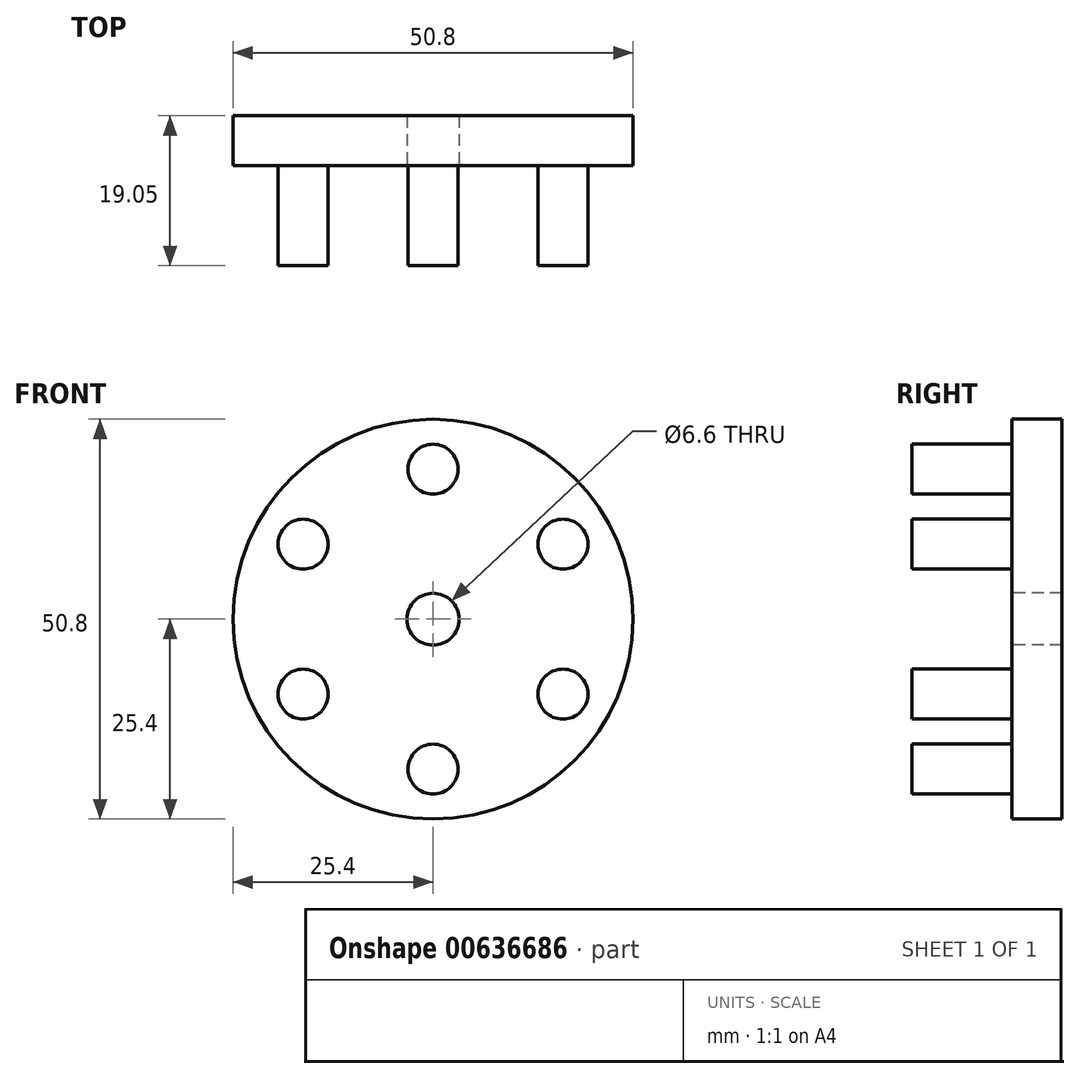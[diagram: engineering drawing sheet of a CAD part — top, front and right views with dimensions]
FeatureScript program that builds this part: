
annotation { "Feature Type Name" : "Feature", "Feature Type Description" : "" }
export const myFeature = defineFeature(function(context is Context, id is Id, definition is map)
    precondition{}
    {
        {
            var Q0;
            Q0=qCreatedBy(makeId("Front.planeOp"),FACE);
            var sketch = newSketch(context, id + "F0", { "sketchPlane" : qUnion([Q0])});
            skCircle(sketch, "E0", {"center": v(0, 0) * mm, "radius": 25.4 * mm});
            skSolve(sketch);
        }
        {
            var Q0;
            Q0 = qSketchRegion(id + "F0", true);
            extrude(context, id + "F1", {"entities" : qUnion([Q0]), "depth" : 6.35 * mm, "offsetDistance" : 25.4 * mm});
        }
        {
            var Q0;
            Q0=makeQuery(id+"F1.opExtrude","CAP_FACE",FACE,{"disambiguationData":[OSD([sQuery(id+"F0.wireOp",EDGE,"E0")])],"isStart":false});
            var sketch = newSketch(context, id + "F2", { "sketchPlane" : qUnion([Q0])});
            skLineSegment(sketch, "E1", {"start": v(0, 25.4) * mm, "end": v(0, 19.05) * mm, "construction": true});
            skCircle(sketch, "E2", {"center": v(0, 19.05) * mm, "radius": 3.18 * mm});
            skCircle(sketch, "E3.1.0", {"center": v(-16.5, 9.53) * mm, "radius": 3.18 * mm});
            skCircle(sketch, "E3.2.0", {"center": v(-16.5, -9.52) * mm, "radius": 3.18 * mm});
            skCircle(sketch, "E3.3.0", {"center": v(0, -19.05) * mm, "radius": 3.18 * mm});
            skCircle(sketch, "E3.4.0", {"center": v(16.5, -9.53) * mm, "radius": 3.18 * mm});
            skCircle(sketch, "E3.5.0", {"center": v(16.5, 9.53) * mm, "radius": 3.18 * mm});
            skPoint(sketch, "E3.center", {"position": v(0, 0) * mm});
            skCircle(sketch, "E4", {"center": v(0, 0) * mm, "radius": 3.3 * mm});
            skSolve(sketch);
        }
        {
            var Q0;
            Q0=makeQuery(id+"F2.imprint","IMPRINT",FACE,{"disambiguationData":[TD([[makeQuery(id+"F2.imprint","IMPRINT",EDGE,{"derivedFrom":sQuery(id+"F2.wireOp",EDGE,"E3.2.0")}),1.0]])]});
            var Q1;
            Q1=makeQuery(id+"F2.imprint","IMPRINT",FACE,{"disambiguationData":[TD([[makeQuery(id+"F2.imprint","IMPRINT",EDGE,{"derivedFrom":sQuery(id+"F2.wireOp",EDGE,"E3.3.0")}),1.0]])]});
            var Q2;
            Q2=makeQuery(id+"F2.imprint","IMPRINT",FACE,{"disambiguationData":[TD([[makeQuery(id+"F2.imprint","IMPRINT",EDGE,{"derivedFrom":sQuery(id+"F2.wireOp",EDGE,"E3.4.0")}),1.0]])]});
            var Q3;
            Q3=makeQuery(id+"F2.imprint","IMPRINT",FACE,{"disambiguationData":[TD([[makeQuery(id+"F2.imprint","IMPRINT",EDGE,{"derivedFrom":sQuery(id+"F2.wireOp",EDGE,"E3.5.0")}),1.0]])]});
            var Q4;
            Q4=makeQuery(id+"F2.imprint","IMPRINT",FACE,{"disambiguationData":[TD([[makeQuery(id+"F2.imprint","IMPRINT",EDGE,{"derivedFrom":sQuery(id+"F2.wireOp",EDGE,"E3.1.0")}),1.0]])]});
            var Q5;
            Q5=makeQuery(id+"F2.imprint","IMPRINT",FACE,{"disambiguationData":[TD([[makeQuery(id+"F2.imprint","IMPRINT",EDGE,{"derivedFrom":sQuery(id+"F2.wireOp",EDGE,"E2")}),1.0]])]});
            extrude(context, id + "F3", {"entities" : qUnion([Q0, Q1, Q2, Q3, Q4, Q5]), "depth" : 12.7 * mm, "offsetDistance" : 25.4 * mm});
        }
        {
            var Q0;
            Q0=makeQuery(id+"F1.opExtrude","CAP_FACE",FACE,{"disambiguationData":[OSD([sQuery(id+"F0.wireOp",EDGE,"E0")])],"isStart":false});
            var sketch = newSketch(context, id + "F4", { "sketchPlane" : qUnion([Q0])});
            skCircle(sketch, "E5", {"center": v(0, 0) * mm, "radius": 3.3 * mm});
            skSolve(sketch);
        }
        {
            var Q0;
            Q0 = qSketchRegion(id + "F4", true);
            extrude(context, id + "F5", {"entities" : qUnion([Q0]), "operationType" : NewBodyOperationType.REMOVE, "oppositeDirection" : true, "depth" : 12.7 * mm, "offsetDistance" : 25.4 * mm});
        }
    });
